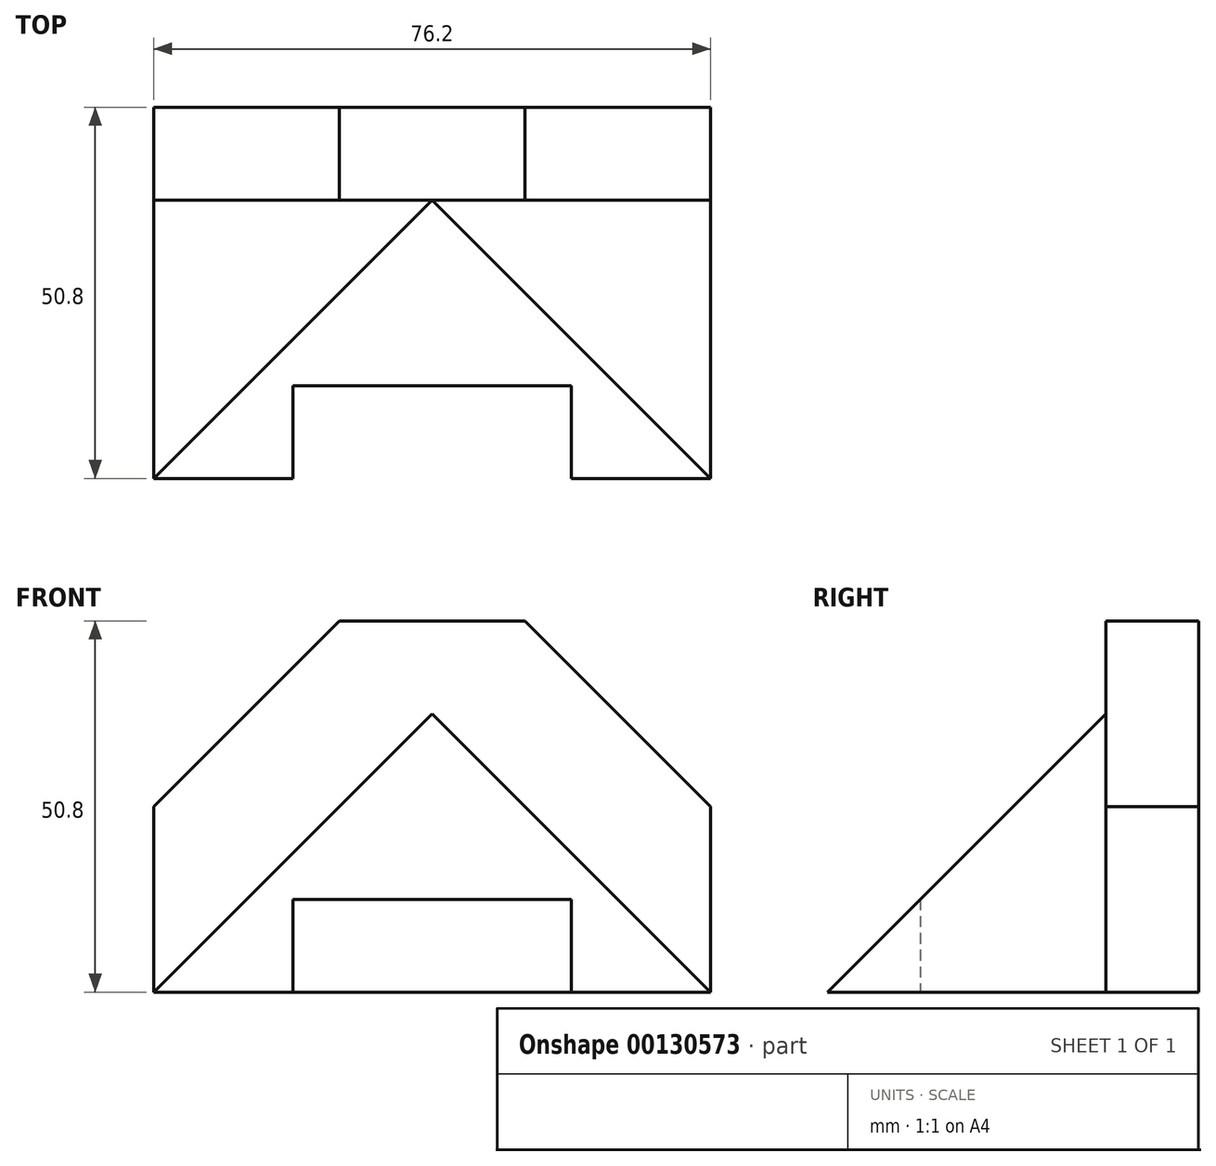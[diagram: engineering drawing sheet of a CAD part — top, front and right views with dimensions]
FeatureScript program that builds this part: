
annotation { "Feature Type Name" : "Feature", "Feature Type Description" : "" }
export const myFeature = defineFeature(function(context is Context, id is Id, definition is map)
    precondition{}
    {
        {
            var Q0;
            Q0=qCreatedBy(makeId("Top.planeOp"),FACE);
            var sketch = newSketch(context, id + "F0", { "sketchPlane" : qUnion([Q0])});
            skLineSegment(sketch, "E0", {"start": v(0, 0) * mm, "end": v(76.2, 0) * mm});
            skLineSegment(sketch, "E1", {"start": v(76.2, 0) * mm, "end": v(76.2, -50.8) * mm});
            skLineSegment(sketch, "E2", {"start": v(76.2, -50.8) * mm, "end": v(57.15, -50.8) * mm});
            skLineSegment(sketch, "E3", {"start": v(57.15, -50.8) * mm, "end": v(57.15, -38.1) * mm});
            skLineSegment(sketch, "E4", {"start": v(57.15, -38.1) * mm, "end": v(19.05, -38.1) * mm});
            skLineSegment(sketch, "E5", {"start": v(19.05, -38.1) * mm, "end": v(19.05, -50.8) * mm});
            skLineSegment(sketch, "E6", {"start": v(19.05, -50.8) * mm, "end": v(0, -50.8) * mm});
            skLineSegment(sketch, "E7", {"start": v(0, -50.8) * mm, "end": v(0, 0) * mm});
            skLineSegment(sketch, "E8", {"start": v(0, -12.7) * mm, "end": v(76.2, -12.7) * mm});
            skLineSegment(sketch, "E9", {"start": v(25.4, 0) * mm, "end": v(25.4, -12.7) * mm});
            skLineSegment(sketch, "E10", {"start": v(50.8, 0) * mm, "end": v(50.8, -12.7) * mm});
            skLineSegment(sketch, "E11", {"start": v(0, -50.8) * mm, "end": v(38.1, -12.7) * mm});
            skLineSegment(sketch, "E12", {"start": v(38.1, -12.7) * mm, "end": v(76.2, -50.8) * mm});
            skLineSegment(sketch, "E13", {"start": v(38.1, 0) * mm, "end": v(38.1, -58.1) * mm, "construction": true});
            skPoint(sketch, "E13.endSnap0", {"position": v(38.1, -38.1) * mm});
            skSolve(sketch);
        }
        {
            var Q0;
            {var subQ3=sQuery(id+"F0.wireOp",EDGE,"E9");Q0=makeQuery(id+"F0.imprint","IMPRINT",FACE,{"disambiguationData":[TD([[makeQuery(id+"F0.imprint","IMPRINT",EDGE,{"derivedFrom":subQ3}),-1.0]])]});}
            var Q1;
            {var subQ3=sQuery(id+"F0.wireOp",EDGE,"E9");Q1=makeQuery(id+"F0.imprint","IMPRINT",FACE,{"disambiguationData":[TD([[makeQuery(id+"F0.imprint","IMPRINT",EDGE,{"derivedFrom":subQ3}),1.0]])]});}
            var Q2;
            {var subQ3=sQuery(id+"F0.wireOp",EDGE,"E10");Q2=makeQuery(id+"F0.imprint","IMPRINT",FACE,{"disambiguationData":[TD([[makeQuery(id+"F0.imprint","IMPRINT",EDGE,{"derivedFrom":subQ3}),1.0]])]});}
            extrude(context, id + "F1", {"entities" : qUnion([Q0, Q1, Q2]), "depth" : 50.8 * mm});
        }
        {
            var Q0;
            Q0=makeQuery(id+"F0.imprint","IMPRINT",FACE,{"disambiguationData":[TD([[makeQuery(id+"F0.imprint","IMPRINT",EDGE,{"derivedFrom":sQuery(id+"F0.wireOp",EDGE,"E2")}),-1.0]])]});
            extrude(context, id + "F2", {"entities" : qUnion([Q0]), "operationType" : NewBodyOperationType.ADD, "depth" : 38.1 * mm});
        }
        {
            var Q0;
            {var subQ0=sQuery(id+"F0.wireOp",EDGE,"E12");Q0=makeQuery(id+"F0.imprint","IMPRINT",FACE,{"disambiguationData":[TD([[makeQuery(id+"F0.imprint","IMPRINT",EDGE,{"derivedFrom":subQ0}),1.0]])]});}
            extrude(context, id + "F3", {"entities" : qUnion([Q0]), "operationType" : NewBodyOperationType.ADD, "depth" : 38.1 * mm});
        }
        {
            var Q0;
            Q0=qCreatedBy(makeId("Right.planeOp"),FACE);
            var sketch = newSketch(context, id + "F4", { "sketchPlane" : qUnion([Q0])});
            skLineSegment(sketch, "E14", {"start": v(0, 0) * mm, "end": v(0, 50.8) * mm});
            skLineSegment(sketch, "E15", {"start": v(0, 50.8) * mm, "end": v(-12.7, 50.8) * mm});
            skLineSegment(sketch, "E16", {"start": v(-12.7, 0) * mm, "end": v(0, 0) * mm});
            skLineSegment(sketch, "E17", {"start": v(-50.8, 0) * mm, "end": v(-50.8, 38.1) * mm});
            skLineSegment(sketch, "E18", {"start": v(-50.8, 38.1) * mm, "end": v(-12.7, 38.1) * mm});
            skLineSegment(sketch, "E19", {"start": v(-50.8, 0) * mm, "end": v(-12.7, 38.1) * mm});
            skLineSegment(sketch, "E20", {"start": v(-12.7, 50.8) * mm, "end": v(-12.7, 0) * mm});
            skLineSegment(sketch, "E21", {"start": v(-50.8, 0) * mm, "end": v(-12.7, 0) * mm});
            skSolve(sketch);
        }
        {
            var Q0;
            {var subQ0=sQuery(id+"F0.wireOp",EDGE,"E11");Q0=makeQuery(id+"F0.imprint","IMPRINT",FACE,{"disambiguationData":[TD([[makeQuery(id+"F0.imprint","IMPRINT",EDGE,{"derivedFrom":subQ0}),1.0]])]});}
            extrude(context, id + "F5", {"entities" : qUnion([Q0]), "operationType" : NewBodyOperationType.ADD, "depth" : 38.1 * mm});
        }
        {
            var Q0;
            Q0=makeQuery(id+"F4.imprint","IMPRINT",FACE,{"disambiguationData":[TD([[makeQuery(id+"F4.imprint","IMPRINT",EDGE,{"derivedFrom":sQuery(id+"F4.wireOp",EDGE,"E17")}),-1.0]])]});
            extrude(context, id + "F6", {"entities" : qUnion([Q0]), "operationType" : NewBodyOperationType.REMOVE, "endBound" : BoundingType.THROUGH_ALL, "depth" : 25.4 * mm});
        }
        {
            var Q0;
            Q0=qCreatedBy(makeId("Front.planeOp"),FACE);
            var sketch = newSketch(context, id + "F7", { "sketchPlane" : qUnion([Q0])});
            skLineSegment(sketch, "E22", {"start": v(0, 0) * mm, "end": v(0, 25.4) * mm});
            skLineSegment(sketch, "E23", {"start": v(0, 25.4) * mm, "end": v(0, 50.8) * mm});
            skLineSegment(sketch, "E24", {"start": v(0, 50.8) * mm, "end": v(25.4, 50.8) * mm});
            skLineSegment(sketch, "E25", {"start": v(25.4, 50.8) * mm, "end": v(50.8, 50.8) * mm});
            skLineSegment(sketch, "E26", {"start": v(50.8, 50.8) * mm, "end": v(76.2, 50.8) * mm});
            skLineSegment(sketch, "E27", {"start": v(76.2, 50.8) * mm, "end": v(76.2, 25.4) * mm});
            skLineSegment(sketch, "E28", {"start": v(76.2, 25.4) * mm, "end": v(76.2, 0) * mm});
            skLineSegment(sketch, "E29", {"start": v(76.2, 0) * mm, "end": v(57.15, 0) * mm});
            skLineSegment(sketch, "E30", {"start": v(57.15, 0) * mm, "end": v(19.05, 0) * mm});
            skLineSegment(sketch, "E31", {"start": v(19.05, 0) * mm, "end": v(0, 0) * mm});
            skLineSegment(sketch, "E32", {"start": v(0, 0) * mm, "end": v(38.1, 38.1) * mm});
            skLineSegment(sketch, "E33", {"start": v(38.1, 38.1) * mm, "end": v(76.2, 0) * mm});
            skLineSegment(sketch, "E34", {"start": v(19.05, 0) * mm, "end": v(19.05, 12.7) * mm});
            skLineSegment(sketch, "E35", {"start": v(19.05, 12.7) * mm, "end": v(57.15, 12.7) * mm});
            skLineSegment(sketch, "E36", {"start": v(57.15, 12.7) * mm, "end": v(57.15, 0) * mm});
            skLineSegment(sketch, "E37", {"start": v(38.1, 50.8) * mm, "end": v(38.1, 0) * mm, "construction": true});
            skLineSegment(sketch, "E38", {"start": v(12.7, 38.1) * mm, "end": v(38.1, 38.1) * mm});
            skLineSegment(sketch, "E39", {"start": v(38.1, 38.1) * mm, "end": v(63.5, 38.1) * mm});
            skLineSegment(sketch, "E40", {"start": v(0, 25.4) * mm, "end": v(12.7, 38.1) * mm});
            skLineSegment(sketch, "E41", {"start": v(12.7, 38.1) * mm, "end": v(25.4, 50.8) * mm});
            skLineSegment(sketch, "E42", {"start": v(76.2, 25.4) * mm, "end": v(63.5, 38.1) * mm});
            skLineSegment(sketch, "E43", {"start": v(50.8, 50.8) * mm, "end": v(63.5, 38.1) * mm});
            skSolve(sketch);
        }
        {
            var Q0;
            Q0=makeQuery(id+"F7.imprint","IMPRINT",FACE,{"disambiguationData":[TD([[makeQuery(id+"F7.imprint","IMPRINT",EDGE,{"derivedFrom":sQuery(id+"F7.wireOp",EDGE,"E23")}),-1.0]])]});
            var Q1;
            Q1=makeQuery(id+"F7.imprint","IMPRINT",FACE,{"disambiguationData":[TD([[makeQuery(id+"F7.imprint","IMPRINT",EDGE,{"derivedFrom":sQuery(id+"F7.wireOp",EDGE,"E26")}),-1.0]])]});
            extrude(context, id + "F8", {"entities" : qUnion([Q0, Q1]), "operationType" : NewBodyOperationType.REMOVE, "endBound" : BoundingType.THROUGH_ALL, "depth" : 25.4 * mm});
        }
        {
            var Q0;
            Q0=makeQuery(id+"F7.imprint","IMPRINT",FACE,{"disambiguationData":[TD([[makeQuery(id+"F7.imprint","IMPRINT",EDGE,{"derivedFrom":sQuery(id+"F7.wireOp",EDGE,"E22")}),-1.0]])]});
            var Q1;
            Q1=sQuery(id+"F7.wireOp",EDGE,"E40");
            var Q2;
            Q2=sQuery(id+"F7.wireOp",EDGE,"E38");
            var Q3;
            Q3=sQuery(id+"F7.wireOp",EDGE,"E32");
            var Q4;
            Q4=sQuery(id+"F7.wireOp",EDGE,"E22");
            extrude(context, id + "F9", {"entities" : qUnion([Q0]), "operationType" : NewBodyOperationType.REMOVE, "surfaceEntities" : qUnion([Q1, Q2, Q3, Q4]), "endBound" : BoundingType.THROUGH_ALL, "depth" : 25.4 * mm, "hasSecondDirection" : true, "secondDirectionOppositeDirection" : false, "secondDirectionDepth" : 12.7 * mm});
        }
        {
            var Q0;
            Q0=makeQuery(id+"F7.imprint","IMPRINT",FACE,{"disambiguationData":[TD([[makeQuery(id+"F7.imprint","IMPRINT",EDGE,{"derivedFrom":sQuery(id+"F7.wireOp",EDGE,"E28")}),-1.0]])]});
            var Q1;
            Q1=sQuery(id+"F7.wireOp",EDGE,"E39");
            var Q2;
            Q2=sQuery(id+"F7.wireOp",EDGE,"E33");
            var Q3;
            Q3=sQuery(id+"F7.wireOp",EDGE,"E28");
            var Q4;
            Q4=sQuery(id+"F7.wireOp",EDGE,"E42");
            extrude(context, id + "F10", {"entities" : qUnion([Q0]), "operationType" : NewBodyOperationType.REMOVE, "surfaceEntities" : qUnion([Q1, Q2, Q3, Q4]), "endBound" : BoundingType.THROUGH_ALL, "depth" : 25.4 * mm, "hasSecondDirection" : true, "secondDirectionOppositeDirection" : false, "secondDirectionDepth" : 12.7 * mm});
        }
    });
